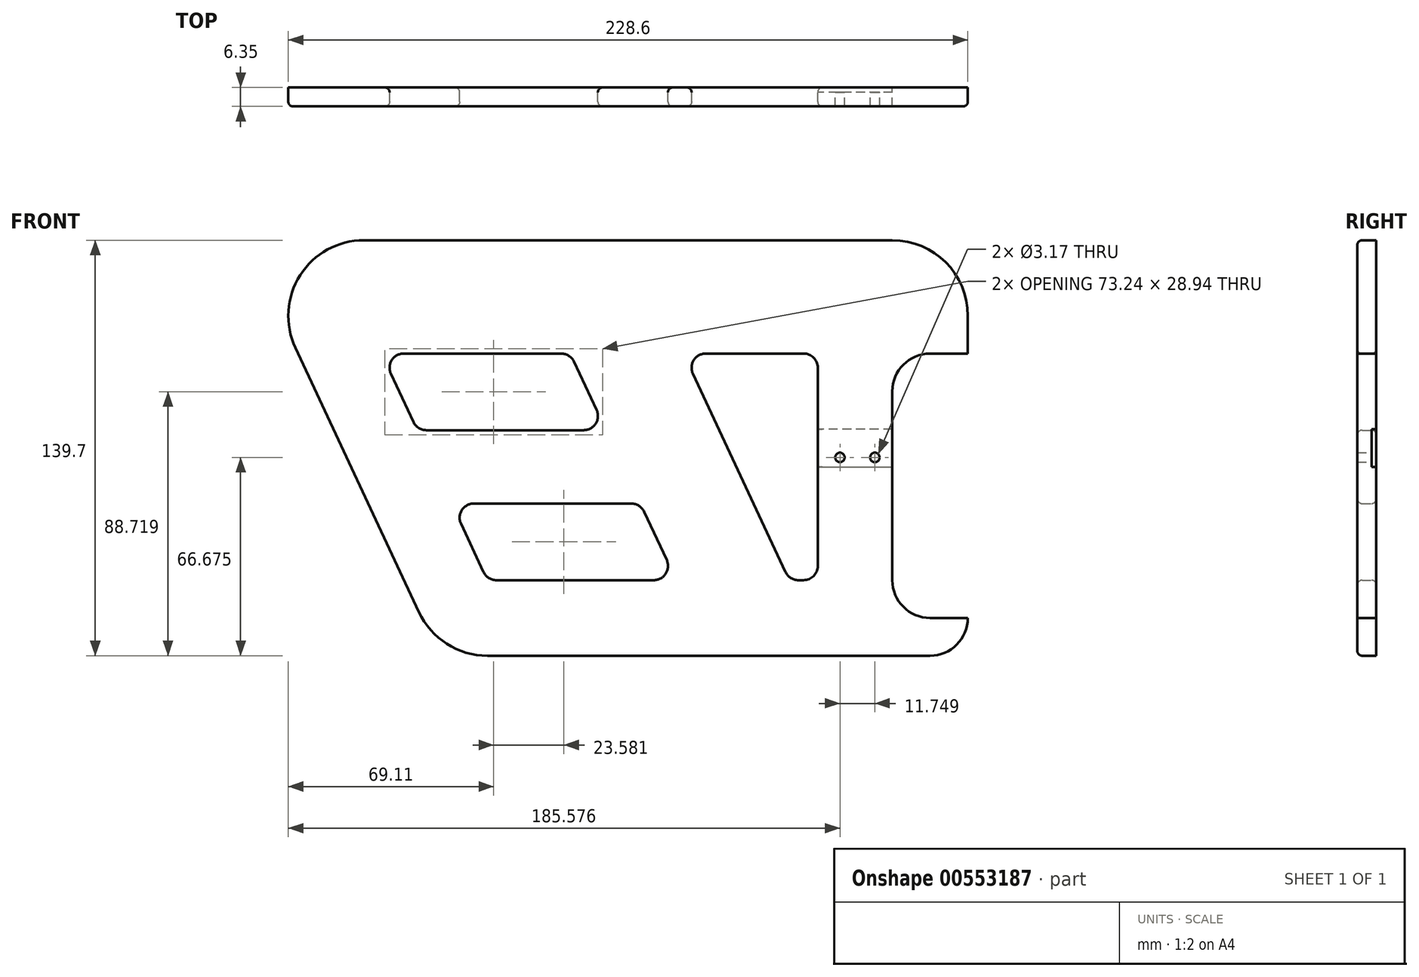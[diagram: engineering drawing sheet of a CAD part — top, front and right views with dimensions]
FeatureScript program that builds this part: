
annotation { "Feature Type Name" : "Feature", "Feature Type Description" : "" }
export const myFeature = defineFeature(function(context is Context, id is Id, definition is map)
    precondition{}
    {
        {
            var Q0;
            Q0=qCreatedBy(makeId("Front.planeOp"),FACE);
            var sketch = newSketch(context, id + "F0", { "sketchPlane" : qUnion([Q0])});
            skLineSegment(sketch, "E0.bottom", {"start": v(88.9, 69.85) * mm, "end": v(-88.9, 69.85) * mm});
            skLineSegment(sketch, "E0.top", {"start": v(114.3, -69.85) * mm, "end": v(-63.5, -69.85) * mm});
            skPoint(sketch, "E0.middle", {"position": v(0, 0) * mm});
            skPoint(sketch, "E1.visualSharp", {"position": v(-114.3, 69.85) * mm});
            skArc(sketch, "E1.filletArc", {"start": v(-88.9, 69.85) * mm, "mid": v(-106.86, 62.41) * mm, "end": v(-114.3, 44.45) * mm});
            skPoint(sketch, "E2.visualSharp", {"position": v(114.3, 69.85) * mm});
            skArc(sketch, "E2.filletArc", {"start": v(114.3, 44.45) * mm, "mid": v(106.86, 62.41) * mm, "end": v(88.9, 69.85) * mm});
            skLineSegment(sketch, "E3", {"start": v(101.6, -69.85) * mm, "end": v(-47.34, -69.85) * mm});
            skArc(sketch, "E4", {"start": v(-88.9, 69.85) * mm, "mid": v(-110.33, 58.09) * mm, "end": v(-111.9, 33.7) * mm});
            skLineSegment(sketch, "E5", {"start": v(-70.35, -55.2) * mm, "end": v(-111.9, 33.7) * mm});
            skPoint(sketch, "E6.orphan", {"position": v(-114.3, -69.85) * mm});
            skPoint(sketch, "E7.visualSharp", {"position": v(-63.5, -69.85) * mm});
            skArc(sketch, "E7.filletArc", {"start": v(-70.35, -55.2) * mm, "mid": v(-60.97, -65.88) * mm, "end": v(-47.34, -69.85) * mm});
            skPoint(sketch, "E8.visualSharp", {"position": v(114.3, -69.85) * mm});
            skArc(sketch, "E8.filletArc", {"start": v(101.6, -69.85) * mm, "mid": v(110.58, -66.13) * mm, "end": v(114.3, -57.15) * mm});
            skLineSegment(sketch, "E9", {"start": v(114.3, -57.15) * mm, "end": v(101.6, -57.15) * mm});
            skLineSegment(sketch, "E10", {"start": v(88.9, -44.45) * mm, "end": v(88.9, 19.05) * mm});
            skPoint(sketch, "E11.visualSharp", {"position": v(88.9, -57.15) * mm});
            skArc(sketch, "E11.filletArc", {"start": v(88.9, -44.45) * mm, "mid": v(92.62, -53.43) * mm, "end": v(101.6, -57.15) * mm});
            skLineSegment(sketch, "E12", {"start": v(-91.13, -10.76) * mm, "end": v(-68.12, 0) * mm, "construction": true});
            skLineSegment(sketch, "E13", {"start": v(-44.3, -44.45) * mm, "end": v(8.66, -44.45) * mm});
            skLineSegment(sketch, "E14", {"start": v(0, -69.85) * mm, "end": v(0, -44.45) * mm, "construction": true});
            skArc(sketch, "E15.filletArc", {"start": v(-48.62, -41.7) * mm, "mid": v(-46.86, -43.7) * mm, "end": v(-44.3, -44.45) * mm});
            skPoint(sketch, "E16.visualSharp", {"position": v(16.16, -44.45) * mm});
            skArc(sketch, "E16.filletArc", {"start": v(8.66, -44.45) * mm, "mid": v(12.69, -42.24) * mm, "end": v(12.99, -37.65) * mm});
            skLineSegment(sketch, "E17", {"start": v(-48.62, -41.7) * mm, "end": v(-56.2, -25.49) * mm});
            skLineSegment(sketch, "E18", {"start": v(-51.88, -18.69) * mm, "end": v(1.08, -18.69) * mm});
            skLineSegment(sketch, "E19.trimOffspring", {"start": v(5.4, -21.44) * mm, "end": v(12.99, -37.65) * mm});
            skPoint(sketch, "E20.visualSharp", {"position": v(-59.38, -18.69) * mm});
            skArc(sketch, "E20.filletArc", {"start": v(-51.88, -18.69) * mm, "mid": v(-55.9, -20.9) * mm, "end": v(-56.2, -25.49) * mm});
            skPoint(sketch, "E21.visualSharp", {"position": v(4.12, -18.69) * mm});
            skArc(sketch, "E21.filletArc", {"start": v(5.4, -21.44) * mm, "mid": v(3.64, -19.43) * mm, "end": v(1.08, -18.69) * mm});
            skLineSegment(sketch, "E22", {"start": v(57.3, -44.45) * mm, "end": v(59.04, -44.45) * mm, "construction": true});
            skLineSegment(sketch, "E23", {"start": v(21.82, 24.95) * mm, "end": v(52.98, -41.7) * mm});
            skLineSegment(sketch, "E24", {"start": v(54.26, -44.45) * mm, "end": v(63.81, -44.45) * mm});
            skLineSegment(sketch, "E25", {"start": v(63.81, -39.67) * mm, "end": v(63.81, 26.97) * mm});
            skLineSegment(sketch, "E26", {"start": v(59.04, 31.75) * mm, "end": v(26.14, 31.75) * mm});
            skArc(sketch, "E27.filletArc", {"start": v(52.98, -41.7) * mm, "mid": v(54.74, -43.7) * mm, "end": v(57.3, -44.45) * mm});
            skArc(sketch, "E28.filletArc", {"start": v(59.04, -44.45) * mm, "mid": v(62.42, -43.05) * mm, "end": v(63.81, -39.67) * mm});
            skLineSegment(sketch, "E29", {"start": v(0, 69.85) * mm, "end": v(0, 31.75) * mm});
            skPoint(sketch, "E29.endSnap0", {"position": v(0, 69.85) * mm});
            skPoint(sketch, "E30.visualSharp", {"position": v(18.64, 31.75) * mm});
            skArc(sketch, "E30.filletArc", {"start": v(26.14, 31.75) * mm, "mid": v(22.11, 29.54) * mm, "end": v(21.82, 24.95) * mm});
            skPoint(sketch, "E31.visualSharp", {"position": v(63.81, 31.75) * mm});
            skArc(sketch, "E31.filletArc", {"start": v(63.81, 26.97) * mm, "mid": v(62.42, 30.35) * mm, "end": v(59.04, 31.75) * mm});
            skLineSegment(sketch, "E32", {"start": v(-46.52, 31.75) * mm, "end": v(-75.46, 31.75) * mm});
            skLineSegment(sketch, "E33", {"start": v(-56.2, -25.49) * mm, "end": v(-59.38, -18.69) * mm});
            skLineSegment(sketch, "E34", {"start": v(-79.78, 24.95) * mm, "end": v(-76.02, 16.9) * mm});
            skArc(sketch, "E35.filletArc", {"start": v(-75.46, 31.75) * mm, "mid": v(-79.49, 29.54) * mm, "end": v(-79.78, 24.95) * mm});
            skLineSegment(sketch, "E36", {"start": v(-10.6, 12.79) * mm, "end": v(-18.18, 29) * mm});
            skLineSegment(sketch, "E37", {"start": v(-67.88, 5.99) * mm, "end": v(-14.92, 5.99) * mm});
            skLineSegment(sketch, "E38.trimOffspring", {"start": v(-72.2, 8.74) * mm, "end": v(-79.78, 24.95) * mm});
            skLineSegment(sketch, "E39", {"start": v(-46.52, 31.75) * mm, "end": v(-22.5, 31.75) * mm});
            skPoint(sketch, "E40.visualSharp", {"position": v(-19.46, 31.75) * mm});
            skArc(sketch, "E40.filletArc", {"start": v(-18.18, 29) * mm, "mid": v(-19.94, 31) * mm, "end": v(-22.5, 31.75) * mm});
            skPoint(sketch, "E41.visualSharp", {"position": v(-7.42, 5.99) * mm});
            skArc(sketch, "E41.filletArc", {"start": v(-14.92, 5.99) * mm, "mid": v(-10.9, 8.2) * mm, "end": v(-10.6, 12.79) * mm});
            skArc(sketch, "E42.filletArc", {"start": v(-72.2, 8.74) * mm, "mid": v(-70.44, 6.73) * mm, "end": v(-67.88, 5.99) * mm});
            skLineSegment(sketch, "E43", {"start": v(114.3, 44.45) * mm, "end": v(114.3, 31.75) * mm});
            skLineSegment(sketch, "E44", {"start": v(101.6, 31.75) * mm, "end": v(114.3, 31.75) * mm});
            skPoint(sketch, "E45.visualSharp", {"position": v(88.9, 31.75) * mm});
            skArc(sketch, "E45.filletArc", {"start": v(101.6, 31.75) * mm, "mid": v(92.62, 28.03) * mm, "end": v(88.9, 19.05) * mm});
            skSolve(sketch);
        }
        {
            var Q0;
            {var subQ4=sQuery(id+"F0.wireOp",EDGE,"E0.bottom");Q0=makeQuery(id+"F0.imprint","IMPRINT",FACE,{"disambiguationData":[TD([[makeQuery(id+"F0.imprint","IMPRINT",EDGE,{"derivedFrom":subQ4}),1.0]])]});}
            extrude(context, id + "F1", {"entities" : qUnion([Q0]), "depth" : 6.35 * mm, "offsetDistance" : 25.4 * mm});
        }
        {
            var Q0;
            Q0=makeQuery(id+"F1.opExtrude","CAP_EDGE",EDGE,{"disambiguationData":[OSD([sQuery(id+"F0.wireOp",EDGE,"E5")])],"isStart":false});
            var Q1;
            Q1=makeQuery(id+"F1.opExtrude","CAP_EDGE",EDGE,{"disambiguationData":[OSD([sQuery(id+"F0.wireOp",EDGE,"E3")])],"isStart":true});
            var Q2;
            Q2=makeQuery(id+"F1.opExtrude","CAP_EDGE",EDGE,{"disambiguationData":[OSD([sQuery(id+"F0.wireOp",EDGE,"6a9c9f40-22be-4694-9eb5-6359758d81a9.filletArc")])],"isStart":false});
            var Q3;
            Q3=makeQuery(id+"F1.opExtrude","CAP_EDGE",EDGE,{"disambiguationData":[OSD([sQuery(id+"F0.wireOp",EDGE,"rLMdYiMk-lrQT-YSmI-KwiX-UnGk6XPE3GuS")])],"isStart":false});
            var Q4;
            Q4=makeQuery(id+"F1.opExtrude","CAP_EDGE",EDGE,{"disambiguationData":[OSD([sQuery(id+"F0.wireOp",EDGE,"E18")])],"isStart":false});
            var Q5;
            Q5=makeQuery(id+"F1.opExtrude","CAP_EDGE",EDGE,{"disambiguationData":[OSD([sQuery(id+"F0.wireOp",EDGE,"E26")])],"isStart":true});
            var Q6;
            Q6=makeQuery(id+"F1.opExtrude","CAP_EDGE",EDGE,{"disambiguationData":[OSD([sQuery(id+"F0.wireOp",EDGE,"rLMdYiMk-lrQT-YSmI-KwiX-UnGk6XPE3GuS")])],"isStart":true});
            var Q7;
            Q7=makeQuery(id+"F1.opExtrude","CAP_EDGE",EDGE,{"disambiguationData":[OSD([sQuery(id+"F0.wireOp",EDGE,"E18")])],"isStart":true});
            var Q8;
            Q8=makeQuery(id+"F1.opExtrude","CAP_EDGE",EDGE,{"disambiguationData":[OSD([sQuery(id+"F0.wireOp",EDGE,"E32"),sQuery(id+"F0.wireOp",EDGE,"E39")])],"isStart":false});
            var Q9;
            Q9=makeQuery(id+"F1.opExtrude","CAP_EDGE",EDGE,{"disambiguationData":[OSD([sQuery(id+"F0.wireOp",EDGE,"E26")])],"isStart":false});
            var Q10;
            Q10=makeQuery(id+"F1.opExtrude","CAP_EDGE",EDGE,{"disambiguationData":[OSD([sQuery(id+"F0.wireOp",EDGE,"E32"),sQuery(id+"F0.wireOp",EDGE,"E39")])],"isStart":true});
            fillet(context, id + "F2", {"entities" : qUnion([Q0, Q1, Q2, Q3, Q4, Q5, Q6, Q7, Q8, Q9, Q10]), "radius" : 1.59 * mm, "tangentPropagation" : true, "allowEdgeOverflow" : false});
        }
        {
            var Q0;
            Q0=makeQuery(id+"F1.opExtrude","CAP_FACE",FACE,{"disambiguationData":[OSD([sQuery(id+"F0.wireOp",EDGE,"E0.bottom"),sQuery(id+"F0.wireOp",EDGE,"E2.filletArc"),sQuery(id+"F0.wireOp",EDGE,"E3"),sQuery(id+"F0.wireOp",EDGE,"E4"),sQuery(id+"F0.wireOp",EDGE,"E5"),sQuery(id+"F0.wireOp",EDGE,"E7.filletArc"),sQuery(id+"F0.wireOp",EDGE,"E8.filletArc"),sQuery(id+"F0.wireOp",EDGE,"E9"),sQuery(id+"F0.wireOp",EDGE,"E10"),sQuery(id+"F0.wireOp",EDGE,"E11.filletArc"),sQuery(id+"F0.wireOp",EDGE,"E13"),sQuery(id+"F0.wireOp",EDGE,"E15.filletArc"),sQuery(id+"F0.wireOp",EDGE,"E16.filletArc"),sQuery(id+"F0.wireOp",EDGE,"E17"),sQuery(id+"F0.wireOp",EDGE,"E18"),sQuery(id+"F0.wireOp",EDGE,"E19.trimOffspring"),sQuery(id+"F0.wireOp",EDGE,"E20.filletArc"),sQuery(id+"F0.wireOp",EDGE,"E21.filletArc"),sQuery(id+"F0.wireOp",EDGE,"E23"),sQuery(id+"F0.wireOp",EDGE,"E24"),sQuery(id+"F0.wireOp",EDGE,"E25"),sQuery(id+"F0.wireOp",EDGE,"E26"),sQuery(id+"F0.wireOp",EDGE,"E27.filletArc"),sQuery(id+"F0.wireOp",EDGE,"E28.filletArc"),sQuery(id+"F0.wireOp",EDGE,"E30.filletArc"),sQuery(id+"F0.wireOp",EDGE,"E31.filletArc"),sQuery(id+"F0.wireOp",EDGE,"E32"),sQuery(id+"F0.wireOp",EDGE,"E35.filletArc"),sQuery(id+"F0.wireOp",EDGE,"E36"),sQuery(id+"F0.wireOp",EDGE,"E37"),sQuery(id+"F0.wireOp",EDGE,"E38.trimOffspring"),sQuery(id+"F0.wireOp",EDGE,"E39"),sQuery(id+"F0.wireOp",EDGE,"E40.filletArc"),sQuery(id+"F0.wireOp",EDGE,"E41.filletArc"),sQuery(id+"F0.wireOp",EDGE,"E42.filletArc"),sQuery(id+"F0.wireOp",EDGE,"E43"),sQuery(id+"F0.wireOp",EDGE,"E44"),sQuery(id+"F0.wireOp",EDGE,"E45.filletArc")])],"isStart":true});
            var sketch = newSketch(context, id + "F3", { "sketchPlane" : qUnion([Q0])});
            skLineSegment(sketch, "E46", {"start": v(-65.4, -6.35) * mm, "end": v(-88.9, -6.35) * mm, "construction": true});
            skLineSegment(sketch, "E47", {"start": v(-88.9, -6.35) * mm, "end": v(-88.9, 6.35) * mm, "construction": true});
            skLineSegment(sketch, "E48", {"start": v(-88.9, 6.35) * mm, "end": v(-65.4, 6.35) * mm, "construction": true});
            skLineSegment(sketch, "E49", {"start": v(-65.4, 6.35) * mm, "end": v(-65.4, -6.35) * mm, "construction": true});
            skLineSegment(sketch, "E50", {"start": v(-88.9, 0) * mm, "end": v(-65.4, 0) * mm, "construction": true});
            skLineSegment(sketch, "E51", {"start": v(-77.15, 0) * mm, "end": v(-65.4, 0) * mm, "construction": true});
            skLineSegment(sketch, "E52", {"start": v(-88.9, 0) * mm, "end": v(-77.15, 0) * mm, "construction": true});
            skLineSegment(sketch, "E53", {"start": v(-83.03, 0) * mm, "end": v(-83.03, -3.17) * mm, "construction": true});
            skLineSegment(sketch, "E54", {"start": v(-71.28, 0) * mm, "end": v(-71.28, -3.17) * mm, "construction": true});
            skCircle(sketch, "E55", {"center": v(-83.03, -3.17) * mm, "radius": 1.59 * mm});
            skCircle(sketch, "E56", {"center": v(-71.28, -3.17) * mm, "radius": 1.59 * mm});
            skSolve(sketch);
        }
        {
            var Q0;
            Q0=makeQuery(id+"F3.imprint","IMPRINT",FACE,{"disambiguationData":[TD([[makeQuery(id+"F3.imprint","IMPRINT",EDGE,{"derivedFrom":sQuery(id+"F3.wireOp",EDGE,"E55")}),1.0]])]});
            var Q1;
            Q1=makeQuery(id+"F3.imprint","IMPRINT",FACE,{"disambiguationData":[TD([[makeQuery(id+"F3.imprint","IMPRINT",EDGE,{"derivedFrom":sQuery(id+"F3.wireOp",EDGE,"E56")}),1.0]])]});
            extrude(context, id + "F4", {"entities" : qUnion([Q0, Q1]), "operationType" : NewBodyOperationType.REMOVE, "oppositeDirection" : true, "depth" : 25.4 * mm, "offsetDistance" : 25.4 * mm});
        }
        {
            var Q0;
            Q0=makeQuery(id+"F1.opExtrude","CAP_FACE",FACE,{"disambiguationData":[OSD([sQuery(id+"F0.wireOp",EDGE,"E0.bottom"),sQuery(id+"F0.wireOp",EDGE,"E2.filletArc"),sQuery(id+"F0.wireOp",EDGE,"E3"),sQuery(id+"F0.wireOp",EDGE,"E4"),sQuery(id+"F0.wireOp",EDGE,"E5"),sQuery(id+"F0.wireOp",EDGE,"E7.filletArc"),sQuery(id+"F0.wireOp",EDGE,"E8.filletArc"),sQuery(id+"F0.wireOp",EDGE,"E9"),sQuery(id+"F0.wireOp",EDGE,"E10"),sQuery(id+"F0.wireOp",EDGE,"E11.filletArc"),sQuery(id+"F0.wireOp",EDGE,"E13"),sQuery(id+"F0.wireOp",EDGE,"E15.filletArc"),sQuery(id+"F0.wireOp",EDGE,"E16.filletArc"),sQuery(id+"F0.wireOp",EDGE,"E17"),sQuery(id+"F0.wireOp",EDGE,"E18"),sQuery(id+"F0.wireOp",EDGE,"E19.trimOffspring"),sQuery(id+"F0.wireOp",EDGE,"E20.filletArc"),sQuery(id+"F0.wireOp",EDGE,"E21.filletArc"),sQuery(id+"F0.wireOp",EDGE,"E23"),sQuery(id+"F0.wireOp",EDGE,"E24"),sQuery(id+"F0.wireOp",EDGE,"E25"),sQuery(id+"F0.wireOp",EDGE,"E26"),sQuery(id+"F0.wireOp",EDGE,"E27.filletArc"),sQuery(id+"F0.wireOp",EDGE,"E28.filletArc"),sQuery(id+"F0.wireOp",EDGE,"E30.filletArc"),sQuery(id+"F0.wireOp",EDGE,"E31.filletArc"),sQuery(id+"F0.wireOp",EDGE,"E32"),sQuery(id+"F0.wireOp",EDGE,"E35.filletArc"),sQuery(id+"F0.wireOp",EDGE,"E36"),sQuery(id+"F0.wireOp",EDGE,"E37"),sQuery(id+"F0.wireOp",EDGE,"E38.trimOffspring"),sQuery(id+"F0.wireOp",EDGE,"E39"),sQuery(id+"F0.wireOp",EDGE,"E40.filletArc"),sQuery(id+"F0.wireOp",EDGE,"E41.filletArc"),sQuery(id+"F0.wireOp",EDGE,"E42.filletArc"),sQuery(id+"F0.wireOp",EDGE,"E43"),sQuery(id+"F0.wireOp",EDGE,"E44"),sQuery(id+"F0.wireOp",EDGE,"E45.filletArc")])],"isStart":true});
            var sketch = newSketch(context, id + "F5", { "sketchPlane" : qUnion([Q0])});
            skLineSegment(sketch, "E57.0", {"start": v(-88.9, 6.35) * mm, "end": v(-65.4, 6.35) * mm});
            skLineSegment(sketch, "E58.0", {"start": v(-88.9, -6.35) * mm, "end": v(-88.9, 6.35) * mm});
            skLineSegment(sketch, "E59.0", {"start": v(-65.4, -6.35) * mm, "end": v(-88.9, -6.35) * mm});
            skLineSegment(sketch, "E60", {"start": v(-65.4, 6.35) * mm, "end": v(-61.63, 6.35) * mm});
            skLineSegment(sketch, "E61", {"start": v(-61.63, 6.35) * mm, "end": v(-61.63, -6.35) * mm});
            skLineSegment(sketch, "E62", {"start": v(-61.63, -6.35) * mm, "end": v(-65.4, -6.35) * mm});
            skSolve(sketch);
        }
        {
            var Q0;
            Q0 = qSketchRegion(id + "F5", true);
            extrude(context, id + "F6", {"entities" : qUnion([Q0]), "operationType" : NewBodyOperationType.REMOVE, "oppositeDirection" : true, "depth" : 1.59 * mm, "offsetDistance" : 25.4 * mm});
        }
    });
